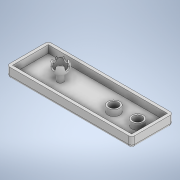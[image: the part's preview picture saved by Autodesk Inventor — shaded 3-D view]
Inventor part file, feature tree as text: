
AUTODESK INVENTOR PART (.ipt)
format: ipt  version: 2021 (Build 250183000, 183)  size: 271,872 bytes
history: native  units: mm
features: sketch x10, extrude x9, fillet x3, revolve x1
ambient origin geometry x8: Origin, YZ Plane, XZ Plane, XY Plane, X Axis, Y Axis, Z Axis, Center Point
bodies: Solid1 (feature_tree)
feature tree (23):
  revolve  "Revolution1"  [1 undecoded]
  extrude  "Extrusion1"  Depth=25.0mm
  fillet  "Fillet1"  [1 undecoded]
  extrude  "Extrusion2"  Depth=3.75mm
  extrude  "Extrusion3"  Depth=50.0mm
  extrude  "Extrusion4"  Depth=50.0mm
  extrude  "Extrusion5"  Depth=50.0mm
  extrude  "Extrusion6"  Depth=5.0mm TaperAngle=0.0deg
  extrude  "Extrusion7"  Depth=17.5mm
  extrude  "Extrusion8"  Depth=5.0mm TaperAngle=0.0deg
  extrude  "Extrusion9"  Depth=5.0mm TaperAngle=0.0deg
  fillet  "Fillet2"  Radius=20.0mm
  fillet  "Fillet3"  Radius=10.0mm
  sketch  "Sketch1"  dims[d0=5.0mm d1=10.0mm]
  sketch  "Sketch2"  dims[d2=25.0mm d3=20.0mm d4=90.0deg]
  sketch  "Sketch3"  dims[d10=7.5mm d11=0.0mm d12=3.75mm]
  sketch  "Sketch4"  dims[d13=50.0mm d14=30.0mm]
  sketch  "Sketch5"  dims[d15=50.0mm d16=30.0mm]
  sketch  "Sketch6"  dims[d17=5.0mm d18=0.0mm d19=50.0mm]
  sketch  "Sketch7"  dims[d20=17.5mm d21=5.0mm d22=0.0mm]
  sketch  "Sketch8"  dims[d23=50.0mm d24=17.5mm]
  sketch  "Sketch9"  dims[d25=5.0mm d26=0.0mm d27=5.0mm d28=0.0mm]
  sketch  "Sketch10"  dims[d29=155.0mm d30=0.0mm d31=5.0mm d32=0.0mm d34=20.0mm d36=10.0mm d37=0.0mm d38=15.0mm d39=10.0mm d40=0.0mm d41=5.0mm d42=5.0mm d33=5.0mm d35=5.0mm]
note: 2 required parameter values undecoded (feature->parameter linkage not recoverable at this tier; creation-order binding heuristic only, values carry confidence <= 0.55)